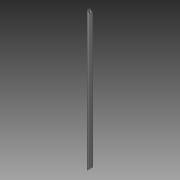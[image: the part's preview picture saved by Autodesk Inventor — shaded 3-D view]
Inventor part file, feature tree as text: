
AUTODESK INVENTOR PART (.ipt)
format: ipt  version: 2019 (Build 230136000, 136)  size: 130,560 bytes
history: native  units: mm
features: extrude x3, sketch x2, projected_geometry x1
ambient origin geometry x8: Origin, YZ Plane, XZ Plane, XY Plane, X Axis, Y Axis, Z Axis, Center Point
bodies: Solid1 (feature_tree)
feature tree (6):
  extrude  "Extrusion1"  Depth=30.0mm
  sketch  "Sketch2"  dims[d2=2.5mm d3=2.5mm d4=1500.0mm d5=0.0mm d6=45.0deg d7=45.0deg d8=0.0mm d9=0.0mm d10=0.0mm d11=0.0mm d12=0.0mm d13=0.0mm]
  extrude  "Extrusion2"  Depth=2.5mm
  extrude  "Extrusion3"  Depth=2.5mm TaperAngle=0.0deg
  sketch  "Sketch1"  dims[d0=30.0mm d1=30.0mm]
  projected_geometry  "Projected Loop1"
